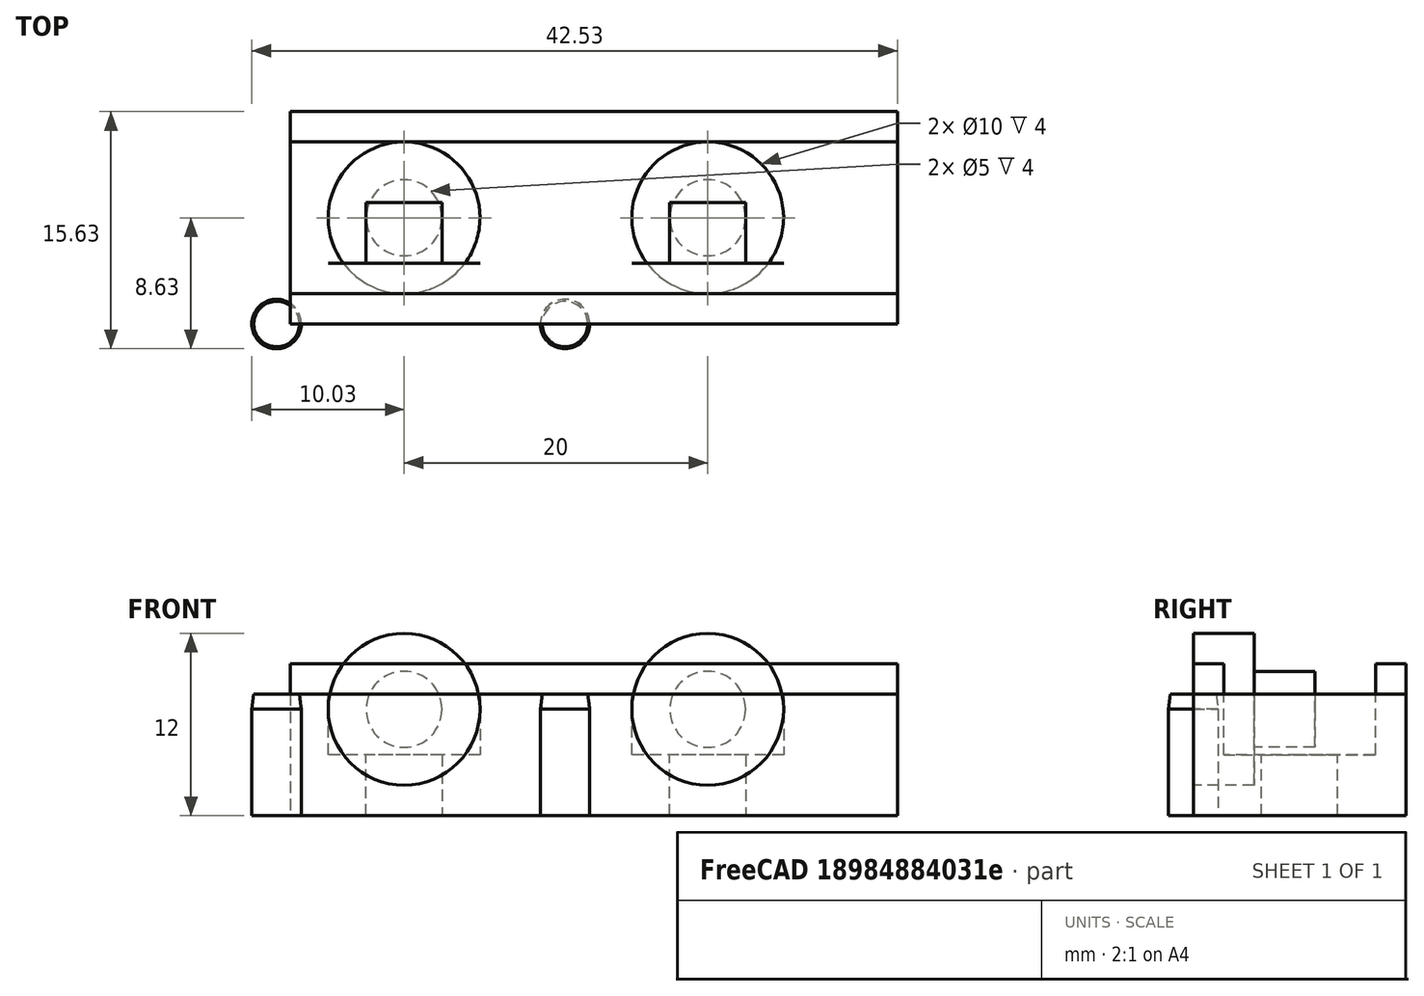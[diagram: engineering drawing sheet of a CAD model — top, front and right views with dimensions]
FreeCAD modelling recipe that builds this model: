
FCSTD DOCUMENT  (FreeCAD 0.20R29603 (Git))
Label: liebherr-freezer-door-sensor-1
License: CC BY-SA 4.0
LicenseURL: https://creativecommons.org/licenses/by-sa/4.0/
objects: Part::Cylinder×6, Part::Part2DObjectPython×4, Part::Box×3, App::Part×3, App::DocumentObjectGroup×2, PartDesign::AdditiveLoft×2, PartDesign::Body×2, Part::Cut×1
note: 20 computed .brp shape members not serialized (recipe doc carries the construction recipe); baked Part::Feature solids carry a one-line shape summary decoded from their .brp

FEATURE [Part::Box] Box  label="Block"
  AttacherType = Attacher::AttachEngine3D
  Height = 14
  Length = 40
  Width = 8
FEATURE [Part::Cylinder] Cylinder  label="Left screw hole (rear)"
  Angle = 360
  AttacherType = Attacher::AttachEngine3D
  FirstAngle = 0
  Height = 4
  Placement = pos=(7.5,4,7) rot=(-1,0,0;1.5708rad)
  Radius = 2.5
  SecondAngle = 0
FEATURE [Part::Cylinder] Cylinder001  label="Right screw hole (rear)"
  Angle = 360
  AttacherType = Attacher::AttachEngine3D
  FirstAngle = 0
  Height = 4
  Placement = pos=(27.5,4,7) rot=(-1,0,0;1.5708rad)
  Radius = 2.5
  SecondAngle = 0
FEATURE [Part::Cylinder] Cylinder002  label="Left screw hole (front)"
  Angle = 360
  AttacherType = Attacher::AttachEngine3D
  FirstAngle = 0
  Height = 4
  Placement = pos=(7.5,0,7) rot=(-1,0,0;1.5708rad)
  Radius = 5
  SecondAngle = 0
FEATURE [App::DocumentObjectGroup] Group  label="Left screw hole"
  Group = -> [Cylinder,Cylinder002]
FEATURE [Part::Cylinder] Cylinder003  label="Right screw hole (front)"
  Angle = 360
  AttacherType = Attacher::AttachEngine3D
  FirstAngle = 0
  Height = 4
  Placement = pos=(27.5,0,7) rot=(-1,0,0;1.5708rad)
  Radius = 5
  SecondAngle = 0
FEATURE [App::DocumentObjectGroup] Group001  label="Right screw hole"
  Group = -> [Cylinder001,Cylinder003]
FEATURE [App::Part] Part  label="Screw holes"
  Group = -> [Cylinder,Cylinder002,Group,Cylinder001,Cylinder003,Group001]
  Origin = -> Origin
FEATURE [Part::Cut] Cut  label="Cut screw holes"
  Base = -> Box
  Placement = pos=(0,0,8) rot=(-1,0,0;1.5708rad)
  Tool = -> Part
FEATURE [Part::Cylinder] Cylinder004  label="Left post"
  Angle = 360
  AttacherType = Attacher::AttachEngine3D
  FirstAngle = 0
  Height = 7
  Placement = pos=(-0.9,0,0) rot=(0,0,1;0rad)
  Radius = 1.625
  SecondAngle = 0
FEATURE [Part::Cylinder] Cylinder005  label="Right post"
  Angle = 360
  AttacherType = Attacher::AttachEngine3D
  FirstAngle = 0
  Height = 7
  Placement = pos=(18.1,0,0) rot=(0,0,1;0rad)
  Radius = 1.625
  SecondAngle = 0
FEATURE [Part::Part2DObjectPython] Circle  label="Left post (rear)"  # Draft 2D object (typed FeaturePython)
  Area = 8.3469
  FirstAngle = 0
  LastAngle = 0
  MakeFace = true
  Placement = pos=(0,0,7) rot=(0,0,1;0rad)
  Radius = 1.63
FEATURE [Part::Part2DObjectPython] Circle001  label="Right post (rear)"  # Draft 2D object (typed FeaturePython)
  Area = 8.3469
  FirstAngle = 0
  LastAngle = 0
  MakeFace = true
  Placement = pos=(19,0,7) rot=(0,0,1;0rad)
  Radius = 1.63
FEATURE [Part::Part2DObjectPython] Circle002  label="Left post (front)"  # Draft 2D object (typed FeaturePython)
  Area = 7.06858
  FirstAngle = 0
  LastAngle = 0
  MakeFace = true
  Placement = pos=(0,0,8) rot=(0,0,1;0rad)
  Radius = 1.5
FEATURE [Part::Part2DObjectPython] Circle003  label="Right post (front)"  # Draft 2D object (typed FeaturePython)
  Area = 7.06858
  FirstAngle = 0
  LastAngle = 0
  MakeFace = true
  Placement = pos=(19,0,8) rot=(0,0,1;0rad)
  Radius = 1.5
FEATURE [PartDesign::AdditiveLoft] AdditiveLoft  label="Left post (loft)"
  Closed = false
  Placement = pos=(0,0,8) rot=(0,0,1;0rad)
  Profile = -> Circle002
  Ruled = false
  Sections = -> [Circle]
FEATURE [PartDesign::Body] Body  label="Left post (body)"
  Group = -> [Circle002,Circle,AdditiveLoft]
  Origin = -> Origin002
  Placement = pos=(-0.9,0,0) rot=(0,0,1;0rad)
  Tip = -> AdditiveLoft
FEATURE [PartDesign::AdditiveLoft] AdditiveLoft001  label="Right post (loft)"
  Closed = false
  Placement = pos=(19,0,8) rot=(0,0,1;0rad)
  Profile = -> Circle003
  Ruled = false
  Sections = -> [Circle001]
FEATURE [PartDesign::Body] Body001  label="Right post (body)"
  Group = -> [Circle003,Circle001,AdditiveLoft001]
  Origin = -> Origin003
  Placement = pos=(-0.9,0,0) rot=(0,0,1;0rad)
  Tip = -> AdditiveLoft001
FEATURE [App::Part] Part001  label="Posts"
  Group = -> [Cylinder004,Cylinder005,Body,Body001]
  Origin = -> Origin001
  Placement = pos=(16,7,8) rot=(0,0,1;0rad)
FEATURE [Part::Box] Box001  label="Guard (top)"
  AttacherType = Attacher::AttachEngine3D
  Height = 2
  Length = 40
  Placement = pos=(0,12,8) rot=(0,0,1;0rad)
  Width = 2
FEATURE [Part::Box] Box002  label="Guard (bottom)"
  AttacherType = Attacher::AttachEngine3D
  Height = 2
  Length = 40
  Placement = pos=(0,0,8) rot=(0,0,1;0rad)
  Width = 2
FEATURE [App::Part] Part002  label="Main"
  Group = -> [Box,Part,Cut,Box001,Box002]
  Origin = -> Origin005
